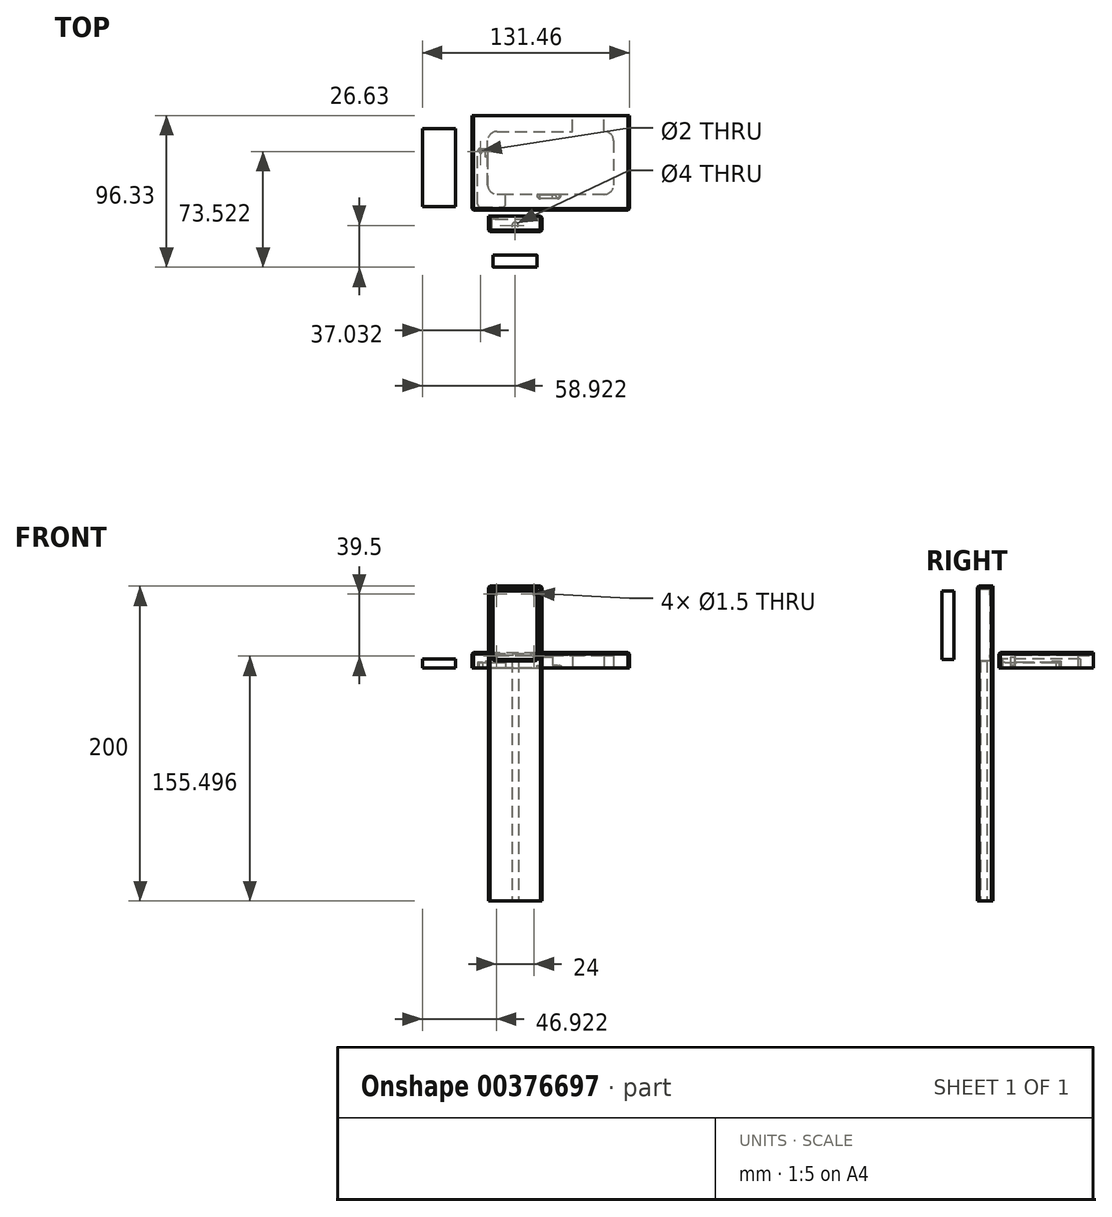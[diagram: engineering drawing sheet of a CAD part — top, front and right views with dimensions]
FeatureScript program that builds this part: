
annotation { "Feature Type Name" : "Feature", "Feature Type Description" : "" }
export const myFeature = defineFeature(function(context is Context, id is Id, definition is map)
    precondition{}
    {
        {
            var Q0;
            Q0=qCreatedBy(makeId("Front.planeOp"),FACE);
            var sketch = newSketch(context, id + "F0", { "sketchPlane" : qUnion([Q0])});
            skLineSegment(sketch, "E0.bottom", {"start": v(-16.56, 49.13) * mm, "end": v(7.44, 49.13) * mm});
            skLineSegment(sketch, "E0.top", {"start": v(-16.56, 5.63) * mm, "end": v(7.44, 5.63) * mm});
            skLineSegment(sketch, "E0.left", {"start": v(-18.56, 47.13) * mm, "end": v(-18.56, 7.63) * mm});
            skLineSegment(sketch, "E0.right", {"start": v(9.44, 47.13) * mm, "end": v(9.44, 7.63) * mm});
            skPoint(sketch, "E1.visualSharp", {"position": v(-18.56, 49.13) * mm});
            skArc(sketch, "E1.filletArc", {"start": v(-16.56, 49.13) * mm, "mid": v(-17.97, 48.54) * mm, "end": v(-18.56, 47.13) * mm});
            skPoint(sketch, "E2.visualSharp", {"position": v(9.44, 49.13) * mm});
            skArc(sketch, "E2.filletArc", {"start": v(9.44, 47.13) * mm, "mid": v(8.86, 48.54) * mm, "end": v(7.44, 49.13) * mm});
            skPoint(sketch, "E3.visualSharp", {"position": v(9.44, 5.63) * mm});
            skArc(sketch, "E3.filletArc", {"start": v(7.44, 5.63) * mm, "mid": v(8.86, 6.21) * mm, "end": v(9.44, 7.63) * mm});
            skPoint(sketch, "E4.visualSharp", {"position": v(-18.56, 5.63) * mm});
            skArc(sketch, "E4.filletArc", {"start": v(-18.56, 7.63) * mm, "mid": v(-17.97, 6.21) * mm, "end": v(-16.56, 5.63) * mm});
            skSolve(sketch);
        }
        {
            var Q0;
            Q0=makeQuery(id+"F0.imprint","IMPRINT",FACE,{"disambiguationData":[TD([[makeQuery(id+"F0.imprint","IMPRINT",EDGE,{"derivedFrom":sQuery(id+"F0.wireOp",EDGE,"E0.bottom")}),-1.0]])]});
            extrude(context, id + "F1", {"entities" : qUnion([Q0]), "depth" : 7.63 * mm});
        }
        {
            var Q0;
            Q0=qCreatedBy(makeId("Top.planeOp"),FACE);
            var sketch = newSketch(context, id + "F2", { "sketchPlane" : qUnion([Q0])});
            skLineSegment(sketch, "E5.bottom", {"start": v(-26.45, 5.51) * mm, "end": v(-12.65, 5.51) * mm});
            skLineSegment(sketch, "E5.top", {"start": v(-26.45, 42.9) * mm, "end": v(-12.65, 42.9) * mm});
            skLineSegment(sketch, "E5.left", {"start": v(-28.45, 7.51) * mm, "end": v(-28.45, 40.9) * mm});
            skLineSegment(sketch, "E5.right", {"start": v(-10.65, 7.51) * mm, "end": v(-10.65, 40.9) * mm});
            skPoint(sketch, "E6.visualSharp", {"position": v(-28.45, 5.51) * mm});
            skArc(sketch, "E6.filletArc", {"start": v(-28.45, 7.51) * mm, "mid": v(-27.86, 6.1) * mm, "end": v(-26.45, 5.51) * mm});
            skPoint(sketch, "E7.visualSharp", {"position": v(-10.65, 5.51) * mm});
            skArc(sketch, "E7.filletArc", {"start": v(-12.65, 5.51) * mm, "mid": v(-11.23, 6.1) * mm, "end": v(-10.65, 7.51) * mm});
            skPoint(sketch, "E8.visualSharp", {"position": v(-10.65, 42.9) * mm});
            skArc(sketch, "E8.filletArc", {"start": v(-10.65, 40.9) * mm, "mid": v(-11.23, 42.3) * mm, "end": v(-12.65, 42.9) * mm});
            skPoint(sketch, "E9.visualSharp", {"position": v(-28.45, 42.9) * mm});
            skArc(sketch, "E9.filletArc", {"start": v(-26.45, 42.9) * mm, "mid": v(-27.86, 42.3) * mm, "end": v(-28.45, 40.9) * mm});
            skCircle(sketch, "E10", {"center": v(-26.45, 40.9) * mm, "radius": 1 * mm});
            skCircle(sketch, "E11", {"center": v(-12.65, 40.9) * mm, "radius": 1 * mm});
            skSolve(sketch);
        }
        {
            var Q0;
            Q0=makeQuery(id+"F2.imprint","IMPRINT",FACE,{"disambiguationData":[TD([[makeQuery(id+"F2.imprint","IMPRINT",EDGE,{"derivedFrom":sQuery(id+"F2.wireOp",EDGE,"E5.bottom")}),1.0]])]});
            extrude(context, id + "F3", {"entities" : qUnion([Q0]), "depth" : 3.68 * mm});
        }
        {
            var Q0;
            Q0=makeQuery(id+"F3.opExtrude","CAP_FACE",FACE,{"disambiguationData":[OSD([sQuery(id+"F2.wireOp",EDGE,"E5.bottom"),sQuery(id+"F2.wireOp",EDGE,"E5.top"),sQuery(id+"F2.wireOp",EDGE,"E5.left"),sQuery(id+"F2.wireOp",EDGE,"E5.right"),sQuery(id+"F2.wireOp",EDGE,"E6.filletArc"),sQuery(id+"F2.wireOp",EDGE,"E7.filletArc"),sQuery(id+"F2.wireOp",EDGE,"E8.filletArc"),sQuery(id+"F2.wireOp",EDGE,"E9.filletArc"),sQuery(id+"F2.wireOp",EDGE,"fOEdSGGO-H9rF-P1pv-IV5H-MRoNtesk1ZPA"),sQuery(id+"F2.wireOp",EDGE,"E10"),sQuery(id+"F2.wireOp",EDGE,"E11"),sQuery(id+"F2.wireOp",EDGE,"7UkpCjGO-dtU7-8SQC-rZuU-JwWnQM4MVfCo")])],"isStart":false});
            var sketch = newSketch(context, id + "F4", { "sketchPlane" : qUnion([Q0])});
            skLineSegment(sketch, "E12.bottom", {"start": v(-15.55, 37.27) * mm, "end": v(-23.55, 37.27) * mm});
            skLineSegment(sketch, "E12.top", {"start": v(-15.55, 42.9) * mm, "end": v(-23.55, 42.9) * mm});
            skLineSegment(sketch, "E12.left", {"start": v(-15.55, 37.27) * mm, "end": v(-15.55, 42.9) * mm});
            skLineSegment(sketch, "E12.right", {"start": v(-23.55, 37.27) * mm, "end": v(-23.55, 42.9) * mm});
            skSolve(sketch);
        }
        {
            var Q0;
            Q0=makeQuery(id+"F4.imprint","IMPRINT",FACE,{"disambiguationData":[TD([[makeQuery(id+"F4.imprint","IMPRINT",EDGE,{"derivedFrom":sQuery(id+"F4.wireOp",EDGE,"E12.bottom")}),-1.0]])]});
            extrude(context, id + "F5", {"entities" : qUnion([Q0]), "operationType" : NewBodyOperationType.ADD, "depth" : (4.5 - 3.68) * mm});
        }
        {
            var Q0;
            Q0=qCreatedBy(makeId("Top.planeOp"),FACE);
            var sketch = newSketch(context, id + "F6", { "sketchPlane" : qUnion([Q0])});
            skLineSegment(sketch, "E13.bottom", {"start": v(22.45, 10.93) * mm, "end": v(11.65, 10.93) * mm});
            skLineSegment(sketch, "E13.top", {"start": v(22.45, 27.6) * mm, "end": v(11.15, 27.6) * mm});
            skLineSegment(sketch, "E13.left", {"start": v(24.45, 12.93) * mm, "end": v(24.45, 25.6) * mm});
            skLineSegment(sketch, "E13.right", {"start": v(9.15, 13.43) * mm, "end": v(9.15, 25.6) * mm});
            skPoint(sketch, "E14.visualSharp", {"position": v(24.45, 10.93) * mm});
            skArc(sketch, "E14.filletArc", {"start": v(22.45, 10.93) * mm, "mid": v(23.86, 11.51) * mm, "end": v(24.45, 12.93) * mm});
            skPoint(sketch, "E15.visualSharp", {"position": v(9.15, 10.93) * mm});
            skArc(sketch, "E15.filletArc", {"start": v(9.15, 13.43) * mm, "mid": v(9.88, 11.66) * mm, "end": v(11.65, 10.93) * mm});
            skPoint(sketch, "E16.visualSharp", {"position": v(9.15, 27.6) * mm});
            skArc(sketch, "E16.filletArc", {"start": v(11.15, 27.6) * mm, "mid": v(9.74, 27.01) * mm, "end": v(9.15, 25.6) * mm});
            skPoint(sketch, "E17.visualSharp", {"position": v(24.45, 27.6) * mm});
            skArc(sketch, "E17.filletArc", {"start": v(24.45, 25.6) * mm, "mid": v(23.86, 27.01) * mm, "end": v(22.45, 27.6) * mm});
            skCircle(sketch, "E18", {"center": v(22.45, 12.93) * mm, "radius": 1.25 * mm});
            skSolve(sketch);
        }
        {
            var Q0;
            Q0=makeQuery(id+"F6.imprint","IMPRINT",FACE,{"disambiguationData":[TD([[makeQuery(id+"F6.imprint","IMPRINT",EDGE,{"derivedFrom":sQuery(id+"F6.wireOp",EDGE,"E13.bottom")}),-1.0]])]});
            extrude(context, id + "F7", {"entities" : qUnion([Q0]), "depth" : 1.67 * mm});
        }
        {
            var Q0;
            Q0=makeQuery(id+"F7.opExtrude","CAP_FACE",FACE,{"disambiguationData":[OSD([sQuery(id+"F6.wireOp",EDGE,"E13.bottom"),sQuery(id+"F6.wireOp",EDGE,"E13.top"),sQuery(id+"F6.wireOp",EDGE,"E13.left"),sQuery(id+"F6.wireOp",EDGE,"E13.right"),sQuery(id+"F6.wireOp",EDGE,"E14.filletArc"),sQuery(id+"F6.wireOp",EDGE,"E15.filletArc"),sQuery(id+"F6.wireOp",EDGE,"E16.filletArc"),sQuery(id+"F6.wireOp",EDGE,"E17.filletArc"),sQuery(id+"F6.wireOp",EDGE,"E18")])],"isStart":false});
            var sketch = newSketch(context, id + "F8", { "sketchPlane" : qUnion([Q0])});
            skLineSegment(sketch, "E19.bottom", {"start": v(11.15, 10.93) * mm, "end": v(19.15, 10.93) * mm});
            skLineSegment(sketch, "E19.top", {"start": v(11.15, 16.93) * mm, "end": v(19.15, 16.93) * mm});
            skLineSegment(sketch, "E19.left", {"start": v(11.15, 10.93) * mm, "end": v(11.15, 16.93) * mm});
            skLineSegment(sketch, "E19.right", {"start": v(19.15, 10.93) * mm, "end": v(19.15, 16.93) * mm});
            skSolve(sketch);
        }
        {
            var Q0;
            {var subQ2=sQuery(id+"F8.wireOp",EDGE,"E19.top");Q0=makeQuery(id+"F8.imprint","IMPRINT",FACE,{"disambiguationData":[TD([[makeQuery(id+"F8.imprint","IMPRINT",EDGE,{"derivedFrom":subQ2}),-1.0]])]});}
            extrude(context, id + "F9", {"entities" : qUnion([Q0]), "operationType" : NewBodyOperationType.ADD, "depth" : 5.6 * mm});
        }
        {
            var Q0;
            Q0=qCreatedBy(makeId("Top.planeOp"),FACE);
            var sketch = newSketch(context, id + "F10", { "sketchPlane" : qUnion([Q0])});
            skLineSegment(sketch, "E20.bottom", {"start": v(-63.48, 55.4) * mm, "end": v(-42.48, 55.4) * mm});
            skLineSegment(sketch, "E20.top", {"start": v(-63.48, 5.9) * mm, "end": v(-42.48, 5.9) * mm});
            skLineSegment(sketch, "E20.left", {"start": v(-63.48, 55.4) * mm, "end": v(-63.48, 5.9) * mm});
            skLineSegment(sketch, "E20.right", {"start": v(-42.48, 55.4) * mm, "end": v(-42.48, 5.9) * mm});
            skSolve(sketch);
        }
        {
            var Q0;
            Q0=makeQuery(id+"F10.imprint","IMPRINT",FACE,{"disambiguationData":[TD([[makeQuery(id+"F10.imprint","IMPRINT",EDGE,{"derivedFrom":sQuery(id+"F10.wireOp",EDGE,"E20.bottom")}),-1.0]])]});
            extrude(context, id + "F11", {"entities" : qUnion([Q0]), "depth" : 6 * mm});
        }
        {
            var Q0;
            Q0=qCreatedBy(makeId("Front.planeOp"),FACE);
            var sketch = newSketch(context, id + "F12", { "sketchPlane" : qUnion([Q0])});
            skLineSegment(sketch, "E21.bottom", {"start": v(-21.56, 52.13) * mm, "end": v(12.44, 52.13) * mm});
            skLineSegment(sketch, "E21.top", {"start": v(-21.56, -147.87) * mm, "end": v(12.44, -147.87) * mm});
            skLineSegment(sketch, "E21.left", {"start": v(-21.56, 52.13) * mm, "end": v(-21.56, -147.87) * mm});
            skLineSegment(sketch, "E21.right", {"start": v(12.44, 52.13) * mm, "end": v(12.44, -147.87) * mm});
            skSolve(sketch);
        }
        {
            var Q0;
            Q0=makeQuery(id+"F12.imprint","IMPRINT",FACE,{"disambiguationData":[TD([[makeQuery(id+"F12.imprint","IMPRINT",EDGE,{"derivedFrom":sQuery(id+"F12.wireOp",EDGE,"E21.bottom")}),-1.0]])]});
            extrude(context, id + "F13", {"entities" : qUnion([Q0]), "depth" : 10 * mm});
        }
        {
            var Q0;
            Q0=makeQuery(id+"F1.opExtrude","SWEPT_BODY",BODY,{"disambiguationData":[OSD([sQuery(id+"F0.wireOp",EDGE,"E0.bottom"),sQuery(id+"F0.wireOp",EDGE,"E0.top"),sQuery(id+"F0.wireOp",EDGE,"E0.left"),sQuery(id+"F0.wireOp",EDGE,"E0.right"),sQuery(id+"F0.wireOp",EDGE,"E1.filletArc"),sQuery(id+"F0.wireOp",EDGE,"E2.filletArc"),sQuery(id+"F0.wireOp",EDGE,"E3.filletArc"),sQuery(id+"F0.wireOp",EDGE,"E4.filletArc"),sQuery(id+"F0.wireOp",EDGE,"38hkBn3J-Whe9-OcH6-mYKZ-11UrIpXxjYj0"),sQuery(id+"F0.wireOp",EDGE,"Z29ZiZuf-8zkg-zRyw-UBm8-Q85509Y2rmHh"),sQuery(id+"F0.wireOp",EDGE,"fbWK4qSt-woi4-nw73-ojh2-E7C9T1qdDKHM"),sQuery(id+"F0.wireOp",EDGE,"34kpA5dJ-Tzsq-JW1U-Yurp-U4r3CrDbEcUA")])]});
            var Q1;
            Q1=makeQuery(id+"F13.opExtrude","SWEPT_EDGE",EDGE,{"disambiguationData":[OSD([sQuery(id+"F12.wireOp",EDGE,"E21.bottom"),sQuery(id+"F12.wireOp",EDGE,"E21.left")])]});
            transform(context, id + "F14", {"entities" : qUnion([Q0]), "transformType" : TransformType.TRANSLATION_DISTANCE, "transformDirection" : qUnion([Q1]), "distance" : 25 * mm, "oppositeDirection" : true, "makeCopy" : false});
        }
        {
            var Q0;
            Q0=makeQuery(id+"F13.opExtrude","CAP_FACE",FACE,{"disambiguationData":[OSD([sQuery(id+"F12.wireOp",EDGE,"E21.bottom"),sQuery(id+"F12.wireOp",EDGE,"E21.top"),sQuery(id+"F12.wireOp",EDGE,"E21.left"),sQuery(id+"F12.wireOp",EDGE,"E21.right")])],"isStart":false});
            var sketch = newSketch(context, id + "F15", { "sketchPlane" : qUnion([Q0])});
            skLineSegment(sketch, "E22.bottom", {"start": v(-16.56, 50.13) * mm, "end": v(7.44, 50.13) * mm});
            skLineSegment(sketch, "E22.top", {"start": v(-16.56, 4.63) * mm, "end": v(7.44, 4.63) * mm});
            skLineSegment(sketch, "E22.left", {"start": v(-19.56, 47.13) * mm, "end": v(-19.56, 7.63) * mm});
            skLineSegment(sketch, "E22.right", {"start": v(10.44, 47.13) * mm, "end": v(10.44, 7.63) * mm});
            skPoint(sketch, "E23.visualSharp", {"position": v(-19.56, 50.13) * mm});
            skArc(sketch, "E23.filletArc", {"start": v(-16.56, 50.13) * mm, "mid": v(-18.68, 49.25) * mm, "end": v(-19.56, 47.13) * mm});
            skPoint(sketch, "E24.visualSharp", {"position": v(10.44, 50.13) * mm});
            skArc(sketch, "E24.filletArc", {"start": v(10.44, 47.13) * mm, "mid": v(9.56, 49.25) * mm, "end": v(7.44, 50.13) * mm});
            skPoint(sketch, "E25.visualSharp", {"position": v(10.44, 4.63) * mm});
            skArc(sketch, "E25.filletArc", {"start": v(7.44, 4.63) * mm, "mid": v(9.56, 5.5) * mm, "end": v(10.44, 7.63) * mm});
            skPoint(sketch, "E26.visualSharp", {"position": v(-19.56, 4.63) * mm});
            skArc(sketch, "E26.filletArc", {"start": v(-19.56, 7.63) * mm, "mid": v(-18.68, 5.5) * mm, "end": v(-16.56, 4.63) * mm});
            skSolve(sketch);
        }
        {
            var Q0;
            Q0=makeQuery(id+"F15.imprint","IMPRINT",FACE,{"disambiguationData":[TD([[makeQuery(id+"F15.imprint","IMPRINT",EDGE,{"derivedFrom":sQuery(id+"F15.wireOp",EDGE,"E22.bottom")}),-1.0]])]});
            extrude(context, id + "F16", {"entities" : qUnion([Q0]), "operationType" : NewBodyOperationType.REMOVE, "oppositeDirection" : true, "depth" : 8 * mm});
        }
        {
            var Q0;
            Q0=makeQuery(id+"F13.opExtrude","SWEPT_FACE",FACE,{"disambiguationData":[OSD([sQuery(id+"F12.wireOp",EDGE,"E21.top")])]});
            var sketch = newSketch(context, id + "F17", { "sketchPlane" : qUnion([Q0])});
            skCircle(sketch, "E27", {"center": v(-4.56, 6) * mm, "radius": 2 * mm});
            skPoint(sketch, "E27.centerSnap0", {"position": v(-4.56, 10) * mm});
            skSolve(sketch);
        }
        {
            var Q0;
            Q0=makeQuery(id+"F17.imprint","IMPRINT",FACE,{"disambiguationData":[TD([[makeQuery(id+"F17.imprint","IMPRINT",EDGE,{"derivedFrom":sQuery(id+"F17.wireOp",EDGE,"E27")}),1.0]])]});
            extrude(context, id + "F18", {"entities" : qUnion([Q0]), "operationType" : NewBodyOperationType.REMOVE, "endBound" : BoundingType.UP_TO_NEXT, "oppositeDirection" : true, "depth" : 25 * mm});
        }
        {
            var Q0;
            Q0=makeQuery(id+"F16.boolean.opBoolean","COPY",FACE,{"derivedFrom":makeQuery(id+"F16.opExtrude","CAP_FACE",FACE,{"disambiguationData":[OSD([sQuery(id+"F15.wireOp",EDGE,"E22.bottom"),sQuery(id+"F15.wireOp",EDGE,"E22.top"),sQuery(id+"F15.wireOp",EDGE,"E22.left"),sQuery(id+"F15.wireOp",EDGE,"E22.right"),sQuery(id+"F15.wireOp",EDGE,"E23.filletArc"),sQuery(id+"F15.wireOp",EDGE,"E24.filletArc"),sQuery(id+"F15.wireOp",EDGE,"E25.filletArc"),sQuery(id+"F15.wireOp",EDGE,"E26.filletArc")])],"isStart":false})});
            var sketch = newSketch(context, id + "F19", { "sketchPlane" : qUnion([Q0])});
            skCircle(sketch, "E28", {"center": v(-16.56, 47.13) * mm, "radius": 0.75 * mm});
            skCircle(sketch, "E29", {"center": v(7.44, 47.13) * mm, "radius": 0.75 * mm});
            skCircle(sketch, "E30", {"center": v(7.44, 7.63) * mm, "radius": 0.75 * mm});
            skCircle(sketch, "E31", {"center": v(-16.56, 7.63) * mm, "radius": 0.75 * mm});
            skSolve(sketch);
        }
        {
            var Q0;
            Q0=makeQuery(id+"F19.imprint","IMPRINT",FACE,{"disambiguationData":[TD([[makeQuery(id+"F19.imprint","IMPRINT",EDGE,{"derivedFrom":sQuery(id+"F19.wireOp",EDGE,"E28")}),1.0]])]});
            var Q1;
            Q1=makeQuery(id+"F19.imprint","IMPRINT",FACE,{"disambiguationData":[TD([[makeQuery(id+"F19.imprint","IMPRINT",EDGE,{"derivedFrom":sQuery(id+"F19.wireOp",EDGE,"E29")}),1.0]])]});
            var Q2;
            Q2=makeQuery(id+"F19.imprint","IMPRINT",FACE,{"disambiguationData":[TD([[makeQuery(id+"F19.imprint","IMPRINT",EDGE,{"derivedFrom":sQuery(id+"F19.wireOp",EDGE,"E30")}),1.0]])]});
            var Q3;
            Q3=makeQuery(id+"F19.imprint","IMPRINT",FACE,{"disambiguationData":[TD([[makeQuery(id+"F19.imprint","IMPRINT",EDGE,{"derivedFrom":sQuery(id+"F19.wireOp",EDGE,"E31")}),1.0]])]});
            extrude(context, id + "F20", {"entities" : qUnion([Q0, Q1, Q2, Q3]), "operationType" : NewBodyOperationType.REMOVE, "endBound" : BoundingType.UP_TO_NEXT, "oppositeDirection" : true, "depth" : 25 * mm});
        }
        {
            var Q0;
            Q0=makeQuery(id+"F13.opExtrude","SWEPT_EDGE",EDGE,{"disambiguationData":[OSD([sQuery(id+"F12.wireOp",EDGE,"E21.bottom"),sQuery(id+"F12.wireOp",EDGE,"E21.right")])]});
            var Q1;
            Q1=makeQuery(id+"F13.opExtrude","CAP_EDGE",EDGE,{"disambiguationData":[OSD([sQuery(id+"F12.wireOp",EDGE,"E21.bottom")])],"isStart":false});
            var Q2;
            Q2=makeQuery(id+"F13.opExtrude","CAP_EDGE",EDGE,{"disambiguationData":[OSD([sQuery(id+"F12.wireOp",EDGE,"E21.right")])],"isStart":false});
            var Q3;
            Q3=makeQuery(id+"F13.opExtrude","CAP_EDGE",EDGE,{"disambiguationData":[OSD([sQuery(id+"F12.wireOp",EDGE,"E21.right")])],"isStart":true});
            var Q4;
            Q4=makeQuery(id+"F13.opExtrude","CAP_EDGE",EDGE,{"disambiguationData":[OSD([sQuery(id+"F12.wireOp",EDGE,"E21.left")])],"isStart":false});
            var Q5;
            Q5=makeQuery(id+"F13.opExtrude","SWEPT_EDGE",EDGE,{"disambiguationData":[OSD([sQuery(id+"F12.wireOp",EDGE,"E21.bottom"),sQuery(id+"F12.wireOp",EDGE,"E21.left")])]});
            chamfer(context, id + "F21", {"entities" : qUnion([Q0, Q1, Q2, Q3, Q4, Q5]), "width" : 1 * mm, "tangentPropagation" : true});
        }
        {
            var Q0;
            Q0=qCreatedBy(makeId("Top.planeOp"),FACE);
            var sketch = newSketch(context, id + "F22", { "sketchPlane" : qUnion([Q0])});
            skLineSegment(sketch, "E32.bottom", {"start": v(-32.02, 63.7) * mm, "end": v(67.98, 63.7) * mm});
            skLineSegment(sketch, "E32.top", {"start": v(-32.02, 3.7) * mm, "end": v(67.98, 3.7) * mm});
            skLineSegment(sketch, "E32.left", {"start": v(-32.02, 63.7) * mm, "end": v(-32.02, 3.7) * mm});
            skLineSegment(sketch, "E32.right", {"start": v(67.98, 63.7) * mm, "end": v(67.98, 3.7) * mm});
            skSolve(sketch);
        }
        {
            var Q0;
            Q0 = qSketchRegion(id + "F22", true);
            extrude(context, id + "F23", {"entities" : qUnion([Q0]), "depth" : 10 * mm});
        }
        {
            var Q0;
            Q0=makeQuery(id+"F23.opExtrude","SWEPT_EDGE",EDGE,{"disambiguationData":[OSD([sQuery(id+"F22.wireOp",EDGE,"E32.top"),sQuery(id+"F22.wireOp",EDGE,"E32.right")])]});
            var Q1;
            Q1=makeQuery(id+"F23.opExtrude","CAP_EDGE",EDGE,{"disambiguationData":[OSD([sQuery(id+"F22.wireOp",EDGE,"E32.right")])],"isStart":false});
            var Q2;
            Q2=makeQuery(id+"F23.opExtrude","CAP_EDGE",EDGE,{"disambiguationData":[OSD([sQuery(id+"F22.wireOp",EDGE,"E32.top")])],"isStart":false});
            var Q3;
            Q3=makeQuery(id+"F23.opExtrude","CAP_EDGE",EDGE,{"disambiguationData":[OSD([sQuery(id+"F22.wireOp",EDGE,"E32.left")])],"isStart":false});
            var Q4;
            Q4=makeQuery(id+"F23.opExtrude","SWEPT_EDGE",EDGE,{"disambiguationData":[OSD([sQuery(id+"F22.wireOp",EDGE,"E32.top"),sQuery(id+"F22.wireOp",EDGE,"E32.left")])]});
            chamfer(context, id + "F24", {"entities" : qUnion([Q0, Q1, Q2, Q3, Q4]), "width" : 1 * mm, "tangentPropagation" : true});
        }
        {
            var Q0;
            Q0=makeQuery(id+"F23.opExtrude","CAP_FACE",FACE,{"disambiguationData":[OSD([sQuery(id+"F22.wireOp",EDGE,"E32.bottom"),sQuery(id+"F22.wireOp",EDGE,"E32.top"),sQuery(id+"F22.wireOp",EDGE,"E32.left"),sQuery(id+"F22.wireOp",EDGE,"E32.right")])],"isStart":true});
            var sketch = newSketch(context, id + "F25", { "sketchPlane" : qUnion([Q0])});
            skLineSegment(sketch, "E33.0", {"start": v(51.98, -13.7) * mm, "end": v(-16.02, -13.7) * mm});
            skLineSegment(sketch, "E33.1", {"start": v(57.98, -47.7) * mm, "end": v(57.98, -19.7) * mm});
            skLineSegment(sketch, "E33.2", {"start": v(-16.02, -53.7) * mm, "end": v(31.98, -53.7) * mm});
            skLineSegment(sketch, "E33.3", {"start": v(-22.02, -19.7) * mm, "end": v(-22.02, -47.7) * mm});
            skPoint(sketch, "E34.visualSharp", {"position": v(-22.02, -13.7) * mm});
            skArc(sketch, "E34.filletArc", {"start": v(-16.02, -13.7) * mm, "mid": v(-20.27, -15.46) * mm, "end": v(-22.02, -19.7) * mm});
            skPoint(sketch, "E35.visualSharp", {"position": v(-22.02, -53.7) * mm});
            skArc(sketch, "E35.filletArc", {"start": v(-22.02, -47.7) * mm, "mid": v(-20.27, -51.94) * mm, "end": v(-16.02, -53.7) * mm});
            skPoint(sketch, "E36.visualSharp", {"position": v(57.98, -53.7) * mm});
            skArc(sketch, "E36.filletArc", {"start": v(51.98, -53.7) * mm, "mid": v(56.22, -51.94) * mm, "end": v(57.98, -47.7) * mm});
            skPoint(sketch, "E37.visualSharp", {"position": v(57.98, -13.7) * mm});
            skArc(sketch, "E37.filletArc", {"start": v(57.98, -19.7) * mm, "mid": v(56.22, -15.46) * mm, "end": v(51.98, -13.7) * mm});
            skLineSegment(sketch, "E38.top", {"start": v(51.98, -63.7) * mm, "end": v(31.98, -63.7) * mm});
            skLineSegment(sketch, "E38.left", {"start": v(51.98, -53.7) * mm, "end": v(51.98, -63.7) * mm});
            skLineSegment(sketch, "E38.right", {"start": v(31.98, -53.7) * mm, "end": v(31.98, -63.7) * mm});
            skSolve(sketch);
        }
        {
            var Q0;
            Q0 = qSketchRegion(id + "F25", true);
            extrude(context, id + "F26", {"entities" : qUnion([Q0]), "operationType" : NewBodyOperationType.REMOVE, "oppositeDirection" : true, "depth" : 8 * mm});
        }
    });
